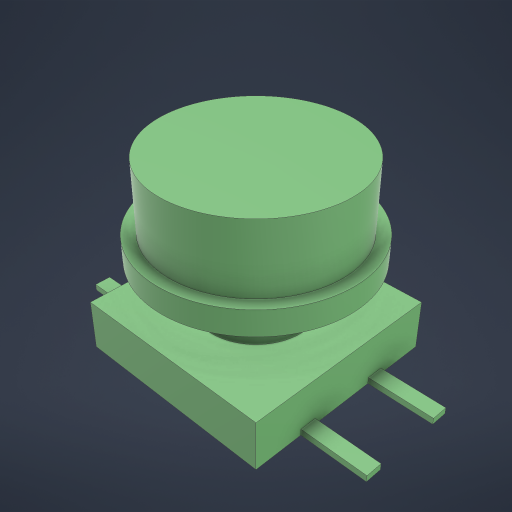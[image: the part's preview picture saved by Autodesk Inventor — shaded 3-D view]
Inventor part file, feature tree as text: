
AUTODESK INVENTOR PART (.ipt)
format: ipt  version: 2023 (Build 270158030, 158C)  size: 253,952 bytes
history: native  units: in
note: dims shown in document units (in); Inventor stores cm internally (conversion verified against a paired STEP export)
features: extrude x5, sketch x5, mirror x1
ambient origin geometry x8: Origin, YZ Plane, XZ Plane, XY Plane, X Axis, Y Axis, Z Axis, Center Point
bodies: Body1 (feature_tree)
feature tree (11):
  extrude  "Extrusion3"  Depth=0.4724in
  extrude  "Extrusion4"  Depth=0.1181in
  extrude  "Extrusion5"  Depth=0.126in
  extrude  "Extrusion6"  Depth=0.0591in
  extrude  "Extrusion7"  Depth=0.2362in
  mirror  "Mirror1"
  sketch  "Sketch3"  dims[d7=0.4724in d8=0.4724in]
  sketch  "Sketch4"  dims[d9=0.1181in d10=0.0in d11=0.2598in]
  sketch  "Sketch5"  dims[d12=0.126in d13=0.0in d14=0.5118in]
  sketch  "Sketch6"  dims[d15=0.0591in d16=0.0in d17=0.4528in]
  sketch  "Sketch7"  dims[d18=0.1614in d19=0.0in d20=0.2362in d21=0.0315in d22=0.1575in d23=0.1575in d24=0.0in]
